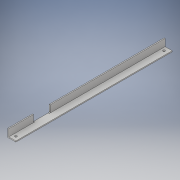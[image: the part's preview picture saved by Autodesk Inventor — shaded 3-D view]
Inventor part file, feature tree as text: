
AUTODESK INVENTOR PART (.ipt)
format: ipt  version: 2017 (Build 210142000, 142)  size: 134,656 bytes
history: native  units: in
note: dims shown in document units (in); Inventor stores cm internally (conversion verified against a paired STEP export)
features: extrude x2, sketch x2, hole x1
ambient origin geometry x8: Origin, YZ Plane, XZ Plane, XY Plane, X Axis, Y Axis, Z Axis, Center Point
bodies: Solid1 (feature_tree)
feature tree (5):
  extrude  "Extrusion1"  Depth=1.0in
  hole  "Hole1"  [1 undecoded]
  extrude  "Extrusion11"  Depth=1.0in
  sketch  "Sketch2"  dims[d0=1.0in d1=1.0in]
  sketch  "Sketch22"  dims[d2=0.125in d3=19.375in d4=0.0in d5=0.5in d6=0.5in d7=0.7874in d9=18.375in d10=0.3937in d12=1.0in d14=0.266in d15=0.75in d16=0.385in d17=0.25in d18=0.5635in d19=1.0in d20=0.8108in d31=0.5in d137=2.0625in d138=3.0625in d139=0.125in d140=1.0in d141=0.0in]
note: 1 required parameter value undecoded (feature->parameter linkage not recoverable at this tier; creation-order binding heuristic only, values carry confidence <= 0.55)
